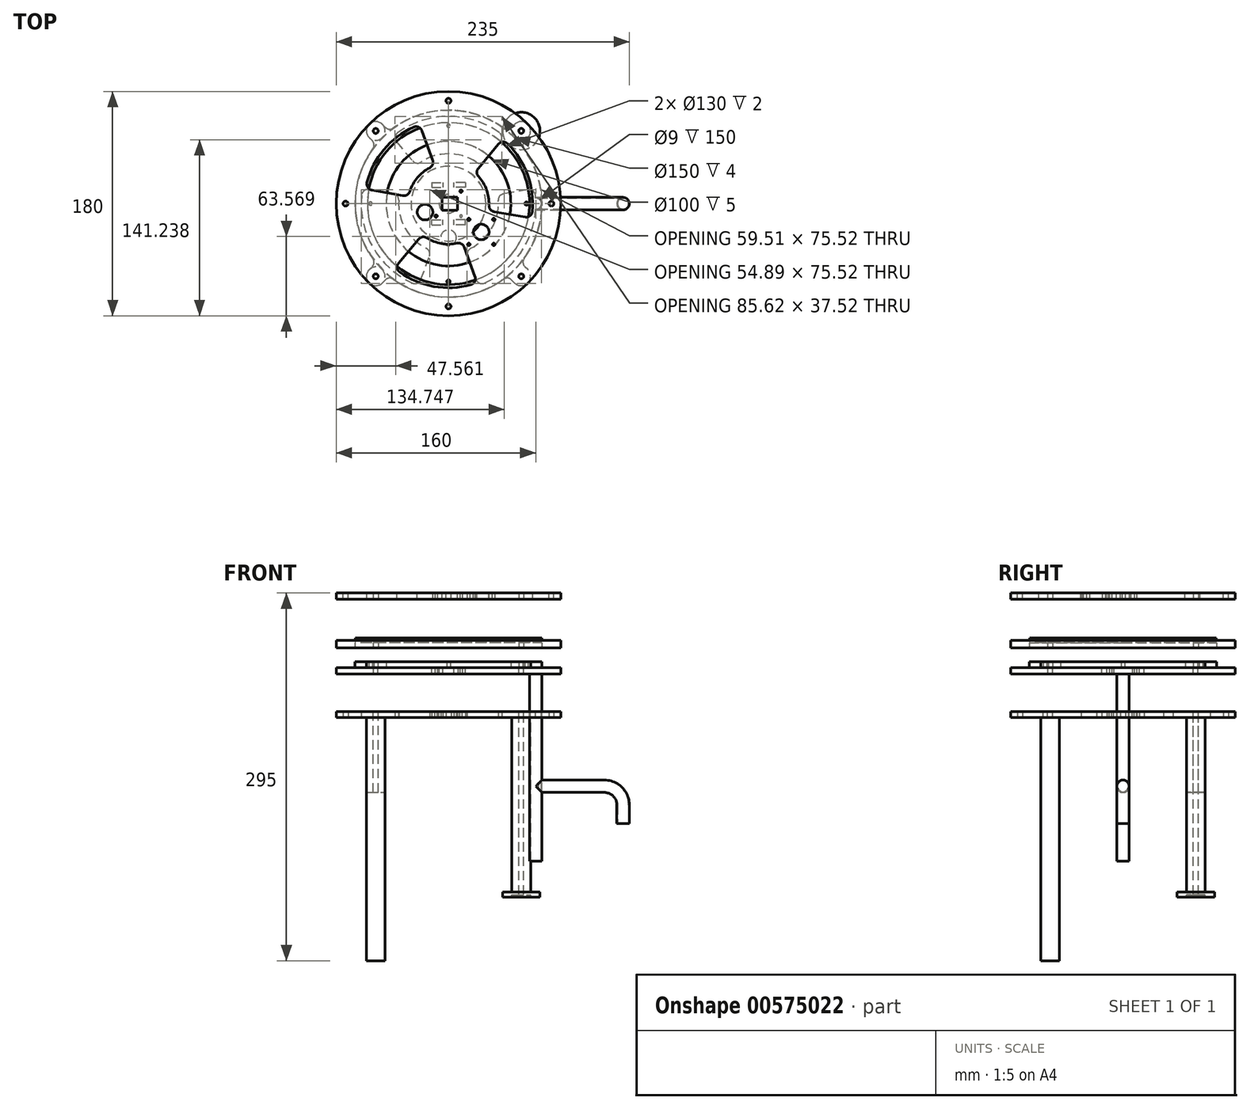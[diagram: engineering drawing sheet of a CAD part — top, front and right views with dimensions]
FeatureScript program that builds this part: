
annotation { "Feature Type Name" : "Feature", "Feature Type Description" : "" }
export const myFeature = defineFeature(function(context is Context, id is Id, definition is map)
    precondition{}
    {
        {
            var Q0;
            Q0=qCreatedBy(makeId("Top.planeOp"),FACE);
            var sketch = newSketch(context, id + "F0", { "sketchPlane" : qUnion([Q0])});
            skCircle(sketch, "E0", {"center": v(0, 0) * mm, "radius": 90 * mm});
            skCircle(sketch, "E1", {"center": v(0, 0) * mm, "radius": 75 * mm});
            skLineSegment(sketch, "E2", {"start": v(-75, 0) * mm, "end": v(-90, 0) * mm, "construction": true});
            skCircle(sketch, "E3", {"center": v(0, 0) * mm, "radius": 82.5 * mm, "construction": true});
            skPoint(sketch, "E4", {"position": v(-82.5, 0) * mm});
            skLineSegment(sketch, "E5", {"start": v(0, 0) * mm, "end": v(-58.34, 58.34) * mm, "construction": true});
            skCircle(sketch, "E6", {"center": v(-58.34, 58.34) * mm, "radius": 2 * mm});
            skCircle(sketch, "E7.MirrorC", {"center": v(58.34, 58.34) * mm, "radius": 2 * mm});
            skCircle(sketch, "E8.MirrorC", {"center": v(-58.34, -58.34) * mm, "radius": 2 * mm});
            skCircle(sketch, "E9.MirrorC", {"center": v(58.34, -58.34) * mm, "radius": 2 * mm});
            skSolve(sketch);
        }
        {
            var Q0;
            Q0=qSketchRegion(id+"F0",true);
            extrude(context, id + "F1", {"entities" : qUnion([Q0]), "depth" : 4 * mm, "offsetDistance" : 25 * mm});
        }
        {
            var Q0;
            Q0=makeQuery(id+"F1.opExtrude","CAP_FACE",FACE,{"disambiguationData":[OSD([sQuery(id+"F0.wireOp",EDGE,"E0"),sQuery(id+"F0.wireOp",EDGE,"E1"),sQuery(id+"F0.wireOp",EDGE,"E6"),sQuery(id+"F0.wireOp",EDGE,"E7.MirrorC"),sQuery(id+"F0.wireOp",EDGE,"E8.MirrorC"),sQuery(id+"F0.wireOp",EDGE,"E9.MirrorC")])],"isStart":true});
            cPlane(context, id + "F2", {"entities" : qUnion([Q0]), "cplaneType" : CPlaneType.OFFSET, "offset" : 1 * mm, "width" : 150 * mm, "height" : 150 * mm});
        }
        {
            var Q0;
            Q0=qCreatedBy(id+"F2.planeOp",FACE);
            var sketch = newSketch(context, id + "F3", { "sketchPlane" : qUnion([Q0])});
            skCircle(sketch, "E10.0", {"center": v(0, 0) * mm, "radius": 90 * mm});
            skCircle(sketch, "E11.0", {"center": v(-58.34, 58.34) * mm, "radius": 2 * mm});
            skCircle(sketch, "E12.0", {"center": v(58.34, 58.34) * mm, "radius": 2 * mm});
            skCircle(sketch, "E13.0", {"center": v(58.34, -58.34) * mm, "radius": 2 * mm});
            skCircle(sketch, "E14.0", {"center": v(-58.34, -58.34) * mm, "radius": 2 * mm});
            skCircle(sketch, "E15", {"center": v(0, 0) * mm, "radius": 7.55 * mm});
            skSolve(sketch);
        }
        {
            var Q0;
            Q0=qSketchRegion(id+"F3",true);
            extrude(context, id + "F4", {"entities" : qUnion([Q0]), "depth" : 5 * mm, "offsetDistance" : 25 * mm});
        }
        {
            var Q0;
            Q0=makeQuery(id+"F4.opExtrude","CAP_FACE",FACE,{"disambiguationData":[OSD([sQuery(id+"F3.wireOp",EDGE,"E10.0"),sQuery(id+"F3.wireOp",EDGE,"E11.0"),sQuery(id+"F3.wireOp",EDGE,"E12.0"),sQuery(id+"F3.wireOp",EDGE,"E13.0"),sQuery(id+"F3.wireOp",EDGE,"E14.0"),sQuery(id+"F3.wireOp",EDGE,"E15")])],"isStart":true});
            var sketch = newSketch(context, id + "F5", { "sketchPlane" : qUnion([Q0])});
            skLineSegment(sketch, "E16.bottom", {"start": v(-10, 10) * mm, "end": v(10, 10) * mm, "construction": true});
            skLineSegment(sketch, "E16.top", {"start": v(-10, -10) * mm, "end": v(10, -10) * mm, "construction": true});
            skLineSegment(sketch, "E16.left", {"start": v(-10, 10) * mm, "end": v(-10, -10) * mm, "construction": true});
            skLineSegment(sketch, "E16.right", {"start": v(10, 10) * mm, "end": v(10, -10) * mm, "construction": true});
            skPoint(sketch, "E16.middle", {"position": v(0, 0) * mm});
            skCircle(sketch, "E17", {"center": v(-10, 10) * mm, "radius": 1 * mm});
            skCircle(sketch, "E18.MirrorC", {"center": v(10, 10) * mm, "radius": 1 * mm});
            skCircle(sketch, "E19.MirrorC", {"center": v(-10, -10) * mm, "radius": 1 * mm});
            skCircle(sketch, "E20.MirrorC", {"center": v(10, -10) * mm, "radius": 1 * mm});
            skSolve(sketch);
        }
        {
            var Q0;
            Q0=qSketchRegion(id+"F5",true);
            extrude(context, id + "F6", {"entities" : qUnion([Q0]), "operationType" : NewBodyOperationType.REMOVE, "endBound" : BoundingType.UP_TO_NEXT, "oppositeDirection" : true, "depth" : 25 * mm, "offsetDistance" : 25 * mm});
        }
        {
            var Q0;
            Q0=makeQuery(id+"F4.opExtrude","CAP_FACE",FACE,{"disambiguationData":[OSD([sQuery(id+"F3.wireOp",EDGE,"E10.0"),sQuery(id+"F3.wireOp",EDGE,"E11.0"),sQuery(id+"F3.wireOp",EDGE,"E12.0"),sQuery(id+"F3.wireOp",EDGE,"E13.0"),sQuery(id+"F3.wireOp",EDGE,"E14.0"),sQuery(id+"F3.wireOp",EDGE,"E15")])],"isStart":false});
            var sketch = newSketch(context, id + "F7", { "sketchPlane" : qUnion([Q0])});
            skPoint(sketch, "E21.center", {"position": v(0, 0) * mm});
            skCircle(sketch, "E22", {"center": v(-58.34, 58.34) * mm, "radius": 7.5 * mm});
            skSolve(sketch);
        }
        {
            var Q0;
            Q0=qSketchRegion(id+"F7",true);
            extrude(context, id + "F8", {"entities" : qUnion([Q0]), "depth" : 195 * mm, "offsetDistance" : 25 * mm});
        }
        {
            var Q0;
            Q0=makeQuery(id+"F4.opExtrude","CAP_FACE",FACE,{"disambiguationData":[OSD([sQuery(id+"F3.wireOp",EDGE,"E10.0"),sQuery(id+"F3.wireOp",EDGE,"E11.0"),sQuery(id+"F3.wireOp",EDGE,"E12.0"),sQuery(id+"F3.wireOp",EDGE,"E13.0"),sQuery(id+"F3.wireOp",EDGE,"E14.0"),sQuery(id+"F3.wireOp",EDGE,"E15")])],"isStart":false});
            cPlane(context, id + "F9", {"entities" : qUnion([Q0]), "cplaneType" : CPlaneType.OFFSET, "offset" : 20 * mm, "oppositeDirection" : true, "width" : 150 * mm, "height" : 150 * mm});
        }
        {
            var Q0;
            Q0=makeQuery(id+"F4.opExtrude","SWEPT_BODY",BODY,{"disambiguationData":[OSD([sQuery(id+"F3.wireOp",EDGE,"E10.0"),sQuery(id+"F3.wireOp",EDGE,"E11.0"),sQuery(id+"F3.wireOp",EDGE,"E12.0"),sQuery(id+"F3.wireOp",EDGE,"E13.0"),sQuery(id+"F3.wireOp",EDGE,"E14.0"),sQuery(id+"F3.wireOp",EDGE,"E15")])]});
            var Q1;
            Q1=qCreatedBy(id+"F9.planeOp",FACE);
            mirror(context, id + "F10", {"entities" : qUnion([Q0]), "mirrorPlane" : qUnion([Q1])});
        }
        {
            var Q0;
            Q0=makeQuery(id+"F10.opPattern","COPY",FACE,{"derivedFrom":makeQuery(id+"F4.opExtrude","CAP_FACE",FACE,{"disambiguationData":[OSD([sQuery(id+"F3.wireOp",EDGE,"E10.0"),sQuery(id+"F3.wireOp",EDGE,"E11.0"),sQuery(id+"F3.wireOp",EDGE,"E12.0"),sQuery(id+"F3.wireOp",EDGE,"E13.0"),sQuery(id+"F3.wireOp",EDGE,"E14.0"),sQuery(id+"F3.wireOp",EDGE,"E15")])],"isStart":false}),"instanceName":"1"});
            var sketch = newSketch(context, id + "F11", { "sketchPlane" : qUnion([Q0])});
            skLineSegment(sketch, "E23.bottom", {"start": v(13, -13) * mm, "end": v(-13, -13) * mm, "construction": true});
            skLineSegment(sketch, "E23.top", {"start": v(13, -17) * mm, "end": v(-13, -17) * mm, "construction": true});
            skLineSegment(sketch, "E23.left", {"start": v(13, -13) * mm, "end": v(13, -17) * mm, "construction": true});
            skLineSegment(sketch, "E23.right", {"start": v(-13, -13) * mm, "end": v(-13, -17) * mm, "construction": true});
            skPoint(sketch, "E23.middle", {"position": v(0, -15) * mm});
            skLineSegment(sketch, "E24", {"start": v(5, -13) * mm, "end": v(5, -17) * mm, "construction": true});
            skLineSegment(sketch, "E25.MirrorCS", {"start": v(-5, -13) * mm, "end": v(-5, -17) * mm, "construction": true});
            skLineSegment(sketch, "E26", {"start": v(5, -13) * mm, "end": v(13, -17) * mm, "construction": true});
            skPoint(sketch, "E27", {"position": v(9, -15) * mm});
            skLineSegment(sketch, "E28.bottom", {"start": v(4.5, -13) * mm, "end": v(13.5, -13) * mm});
            skLineSegment(sketch, "E28.top", {"start": v(4.5, -17) * mm, "end": v(13.5, -17) * mm});
            skLineSegment(sketch, "E28.left", {"start": v(4.5, -13) * mm, "end": v(4.5, -17) * mm});
            skLineSegment(sketch, "E28.right", {"start": v(13.5, -13) * mm, "end": v(13.5, -17) * mm});
            skLineSegment(sketch, "E29.MirrorCS", {"start": v(-4.5, -13) * mm, "end": v(-4.5, -17) * mm});
            skLineSegment(sketch, "E30.MirrorCS", {"start": v(-4.5, -13) * mm, "end": v(-13.5, -13) * mm});
            skLineSegment(sketch, "E31.MirrorCS", {"start": v(-13.5, -13) * mm, "end": v(-13.5, -17) * mm});
            skLineSegment(sketch, "E32.MirrorCS", {"start": v(-4.5, -17) * mm, "end": v(-13.5, -17) * mm});
            skLineSegment(sketch, "E33.MirrorCS", {"start": v(-13.5, 13) * mm, "end": v(-13.5, 17) * mm});
            skLineSegment(sketch, "E34.MirrorCS", {"start": v(-4.5, 13) * mm, "end": v(-13.5, 13) * mm});
            skLineSegment(sketch, "E35.MirrorCS", {"start": v(-4.5, 13) * mm, "end": v(-4.5, 17) * mm});
            skLineSegment(sketch, "E36.MirrorCS", {"start": v(-4.5, 17) * mm, "end": v(-13.5, 17) * mm});
            skLineSegment(sketch, "E37.MirrorCS", {"start": v(4.5, 13) * mm, "end": v(4.5, 17) * mm});
            skLineSegment(sketch, "E38.MirrorCS", {"start": v(4.5, 13) * mm, "end": v(13.5, 13) * mm});
            skLineSegment(sketch, "E39.MirrorCS", {"start": v(13.5, 13) * mm, "end": v(13.5, 17) * mm});
            skLineSegment(sketch, "E40.MirrorCS", {"start": v(4.5, 17) * mm, "end": v(13.5, 17) * mm});
            skSolve(sketch);
        }
        {
            var Q0;
            Q0=qSketchRegion(id+"F11",true);
            extrude(context, id + "F12", {"entities" : qUnion([Q0]), "operationType" : NewBodyOperationType.REMOVE, "endBound" : BoundingType.UP_TO_NEXT, "oppositeDirection" : true, "depth" : 25 * mm, "offsetDistance" : 25 * mm});
        }
        {
            var Q0;
            Q0=makeQuery(id+"F10.opPattern","COPY",FACE,{"derivedFrom":makeQuery(id+"F4.opExtrude","CAP_FACE",FACE,{"disambiguationData":[OSD([sQuery(id+"F3.wireOp",EDGE,"E10.0"),sQuery(id+"F3.wireOp",EDGE,"E11.0"),sQuery(id+"F3.wireOp",EDGE,"E12.0"),sQuery(id+"F3.wireOp",EDGE,"E13.0"),sQuery(id+"F3.wireOp",EDGE,"E14.0"),sQuery(id+"F3.wireOp",EDGE,"E15")])],"isStart":false}),"instanceName":"1"});
            var sketch = newSketch(context, id + "F13", { "sketchPlane" : qUnion([Q0])});
            skCircle(sketch, "E41", {"center": v(-58.34, 58.34) * mm, "radius": 1.85 * mm});
            skCircle(sketch, "E42.0", {"center": v(-58.34, 58.34) * mm, "radius": 2 * mm});
            skCircle(sketch, "E43.1.0", {"center": v(-58.34, -58.34) * mm, "radius": 1.85 * mm});
            skCircle(sketch, "E43.1.1", {"center": v(-58.34, -58.34) * mm, "radius": 2 * mm});
            skCircle(sketch, "E43.2.0", {"center": v(58.34, -58.34) * mm, "radius": 1.85 * mm});
            skCircle(sketch, "E43.2.1", {"center": v(58.34, -58.34) * mm, "radius": 2 * mm});
            skCircle(sketch, "E43.3.0", {"center": v(58.34, 58.34) * mm, "radius": 1.85 * mm});
            skCircle(sketch, "E43.3.1", {"center": v(58.34, 58.34) * mm, "radius": 2 * mm});
            skPoint(sketch, "E43.center", {"position": v(0, 0) * mm});
            skSolve(sketch);
        }
        {
            var Q0;
            Q0=qSketchRegion(id+"F13",true);
            var Q1;
            Q1=makeQuery(id+"F10.opPattern","COPY",FACE,{"derivedFrom":makeQuery(id+"F4.opExtrude","CAP_FACE",FACE,{"disambiguationData":[OSD([sQuery(id+"F3.wireOp",EDGE,"E10.0"),sQuery(id+"F3.wireOp",EDGE,"E11.0"),sQuery(id+"F3.wireOp",EDGE,"E12.0"),sQuery(id+"F3.wireOp",EDGE,"E13.0"),sQuery(id+"F3.wireOp",EDGE,"E14.0"),sQuery(id+"F3.wireOp",EDGE,"E15")])],"isStart":true}),"instanceName":"1"});
            extrude(context, id + "F14", {"entities" : qUnion([Q0]), "operationType" : NewBodyOperationType.ADD, "endBound" : BoundingType.UP_TO_SURFACE, "oppositeDirection" : true, "depth" : 25 * mm, "endBoundEntityFace" : qUnion([Q1]), "offsetDistance" : 25 * mm});
        }
        {
            var Q0;
            Q0=makeQuery(id+"F14.boolean.opBoolean","MERGE",FACE,{"derivedFrom":[makeQuery(id+"F10.opPattern","COPY",FACE,{"derivedFrom":makeQuery(id+"F4.opExtrude","CAP_FACE",FACE,{"disambiguationData":[OSD([sQuery(id+"F3.wireOp",EDGE,"E10.0"),sQuery(id+"F3.wireOp",EDGE,"E11.0"),sQuery(id+"F3.wireOp",EDGE,"E12.0"),sQuery(id+"F3.wireOp",EDGE,"E13.0"),sQuery(id+"F3.wireOp",EDGE,"E14.0"),sQuery(id+"F3.wireOp",EDGE,"E15")])],"isStart":false}),"instanceName":"1"}),makeQuery(id+"F14.opExtrude","CAP_FACE",FACE,{"disambiguationData":[OSD([sQuery(id+"F13.wireOp",EDGE,"E41"),sQuery(id+"F13.wireOp",EDGE,"E42.0")])],"isStart":true}),makeQuery(id+"F14.opExtrude","CAP_FACE",FACE,{"disambiguationData":[OSD([sQuery(id+"F13.wireOp",EDGE,"E43.1.0"),sQuery(id+"F13.wireOp",EDGE,"E43.1.1")])],"isStart":true}),makeQuery(id+"F14.opExtrude","CAP_FACE",FACE,{"disambiguationData":[OSD([sQuery(id+"F13.wireOp",EDGE,"E43.2.0"),sQuery(id+"F13.wireOp",EDGE,"E43.2.1")])],"isStart":true}),makeQuery(id+"F14.opExtrude","CAP_FACE",FACE,{"disambiguationData":[OSD([sQuery(id+"F13.wireOp",EDGE,"E43.3.0"),sQuery(id+"F13.wireOp",EDGE,"E43.3.1")])],"isStart":true})]});
            var sketch = newSketch(context, id + "F15", { "sketchPlane" : qUnion([Q0])});
            skCircle(sketch, "E44.0", {"center": v(-58.34, 58.34) * mm, "radius": 1.85 * mm});
            skCircle(sketch, "E45.0", {"center": v(-58.34, -58.34) * mm, "radius": 1.85 * mm});
            skCircle(sketch, "E46.0", {"center": v(58.34, -58.34) * mm, "radius": 1.85 * mm});
            skCircle(sketch, "E47.0", {"center": v(58.34, 58.34) * mm, "radius": 1.85 * mm});
            skArc(sketch, "E48", {"start": v(63.64, 53.03) * mm, "mid": v(63.64, 63.64) * mm, "end": v(53.03, 63.64) * mm});
            skCircle(sketch, "E49", {"center": v(0, 0) * mm, "radius": 50 * mm});
            skArc(sketch, "E50", {"start": v(47.46, 58.07) * mm, "mid": v(0, 75) * mm, "end": v(-47.46, 58.07) * mm});
            skLineSegment(sketch, "E51", {"start": v(58.34, 58.34) * mm, "end": v(63.64, 53.03) * mm, "construction": true});
            skLineSegment(sketch, "E52", {"start": v(58.34, 58.34) * mm, "end": v(0, 0) * mm, "construction": true});
            skLineSegment(sketch, "E53", {"start": v(63.64, 53.03) * mm, "end": v(58.07, 47.46) * mm});
            skLineSegment(sketch, "E54.MirrorCS", {"start": v(53.03, 63.64) * mm, "end": v(47.46, 58.07) * mm});
            skLineSegment(sketch, "E55.MirrorCS", {"start": v(-53.03, 63.64) * mm, "end": v(-47.46, 58.07) * mm});
            skArc(sketch, "E56.MirrorCS", {"start": v(-63.64, 53.03) * mm, "mid": v(-63.64, 63.64) * mm, "end": v(-53.03, 63.64) * mm});
            skLineSegment(sketch, "E57.MirrorCS", {"start": v(-63.64, 53.03) * mm, "end": v(-58.07, 47.46) * mm});
            skLineSegment(sketch, "E58.MirrorCS", {"start": v(58.34, -58.34) * mm, "end": v(59.64, -57.03) * mm, "construction": true});
            skLineSegment(sketch, "E59.MirrorCS", {"start": v(-63.64, -53.03) * mm, "end": v(-58.07, -47.46) * mm});
            skLineSegment(sketch, "E60.MirrorCS", {"start": v(63.64, -53.03) * mm, "end": v(58.07, -47.46) * mm});
            skArc(sketch, "E61.MirrorCS", {"start": v(63.64, -53.03) * mm, "mid": v(63.64, -63.64) * mm, "end": v(53.03, -63.64) * mm});
            skLineSegment(sketch, "E62.MirrorCS", {"start": v(53.03, -63.64) * mm, "end": v(47.46, -58.07) * mm});
            skLineSegment(sketch, "E63.MirrorCS", {"start": v(-53.03, -63.64) * mm, "end": v(-47.46, -58.07) * mm});
            skArc(sketch, "E64.MirrorCS", {"start": v(-63.64, -53.03) * mm, "mid": v(-63.64, -63.64) * mm, "end": v(-53.03, -63.64) * mm});
            skArc(sketch, "E65.trimOffspring", {"start": v(-58.07, 47.46) * mm, "mid": v(-75, 0) * mm, "end": v(-58.07, -47.46) * mm});
            skArc(sketch, "E66.trimOffspring", {"start": v(-47.46, -58.07) * mm, "mid": v(0, -75) * mm, "end": v(47.46, -58.07) * mm});
            skArc(sketch, "E67.trimOffspring", {"start": v(58.07, -47.46) * mm, "mid": v(75, 0) * mm, "end": v(58.07, 47.46) * mm});
            skCircle(sketch, "E68", {"center": v(0, 62.5) * mm, "radius": 1.35 * mm});
            skCircle(sketch, "E69.1.0", {"center": v(-62.5, 0) * mm, "radius": 1.35 * mm});
            skCircle(sketch, "E69.2.0", {"center": v(0, -62.5) * mm, "radius": 1.35 * mm});
            skCircle(sketch, "E70.1.3.0", {"center": v(62.5, 0) * mm, "radius": 1.35 * mm});
            skSolve(sketch);
        }
        {
            var Q0;
            Q0=qSketchRegion(id+"F15",true);
            extrude(context, id + "F16", {"entities" : qUnion([Q0]), "depth" : 5 * mm, "offsetDistance" : 25 * mm});
        }
        {
            var Q0;
            Q0=makeQuery(id+"F16.opExtrude","SWEPT_EDGE",EDGE,{"disambiguationData":[OSD([sQuery(id+"F15.wireOp",EDGE,"E50"),sQuery(id+"F15.wireOp",EDGE,"E55.MirrorCS")])]});
            var Q1;
            Q1=makeQuery(id+"F16.opExtrude","SWEPT_EDGE",EDGE,{"disambiguationData":[OSD([sQuery(id+"F15.wireOp",EDGE,"E50"),sQuery(id+"F15.wireOp",EDGE,"E54.MirrorCS")])]});
            var Q2;
            Q2=makeQuery(id+"F16.opExtrude","SWEPT_EDGE",EDGE,{"disambiguationData":[OSD([sQuery(id+"F15.wireOp",EDGE,"E53"),sQuery(id+"F15.wireOp",EDGE,"E67.trimOffspring")])]});
            var Q3;
            Q3=makeQuery(id+"F16.opExtrude","SWEPT_EDGE",EDGE,{"disambiguationData":[OSD([sQuery(id+"F15.wireOp",EDGE,"E60.MirrorCS"),sQuery(id+"F15.wireOp",EDGE,"E67.trimOffspring")])]});
            var Q4;
            Q4=makeQuery(id+"F16.opExtrude","SWEPT_EDGE",EDGE,{"disambiguationData":[OSD([sQuery(id+"F15.wireOp",EDGE,"E62.MirrorCS"),sQuery(id+"F15.wireOp",EDGE,"E66.trimOffspring")])]});
            var Q5;
            Q5=makeQuery(id+"F16.opExtrude","SWEPT_EDGE",EDGE,{"disambiguationData":[OSD([sQuery(id+"F15.wireOp",EDGE,"E63.MirrorCS"),sQuery(id+"F15.wireOp",EDGE,"E66.trimOffspring")])]});
            var Q6;
            Q6=makeQuery(id+"F16.opExtrude","SWEPT_EDGE",EDGE,{"disambiguationData":[OSD([sQuery(id+"F15.wireOp",EDGE,"E59.MirrorCS"),sQuery(id+"F15.wireOp",EDGE,"E65.trimOffspring")])]});
            var Q7;
            Q7=makeQuery(id+"F16.opExtrude","SWEPT_EDGE",EDGE,{"disambiguationData":[OSD([sQuery(id+"F15.wireOp",EDGE,"E57.MirrorCS"),sQuery(id+"F15.wireOp",EDGE,"E65.trimOffspring")])]});
            fillet(context, id + "F17", {"entities" : qUnion([Q0, Q1, Q2, Q3, Q4, Q5, Q6, Q7]), "radius" : 5 * mm, "tangentPropagation" : true, "allowEdgeOverflow" : false});
        }
        {
            var Q0;
            Q0=makeQuery(id+"F4.opExtrude","CAP_FACE",FACE,{"disambiguationData":[OSD([sQuery(id+"F3.wireOp",EDGE,"E10.0"),sQuery(id+"F3.wireOp",EDGE,"E11.0"),sQuery(id+"F3.wireOp",EDGE,"E12.0"),sQuery(id+"F3.wireOp",EDGE,"E13.0"),sQuery(id+"F3.wireOp",EDGE,"E14.0"),sQuery(id+"F3.wireOp",EDGE,"E15")])],"isStart":false});
            var sketch = newSketch(context, id + "F18", { "sketchPlane" : qUnion([Q0])});
            skCircle(sketch, "E71", {"center": v(58.34, -58.34) * mm, "radius": 7.5 * mm});
            skCircle(sketch, "E72.0", {"center": v(58.34, -58.34) * mm, "radius": 2 * mm});
            skSolve(sketch);
        }
        {
            var Q0;
            Q0=qSketchRegion(id+"F18",true);
            extrude(context, id + "F19", {"entities" : qUnion([Q0]), "depth" : 140 * mm, "offsetDistance" : 25 * mm});
        }
        {
            var Q0;
            Q0=makeQuery(id+"F19.opExtrude","CAP_FACE",FACE,{"disambiguationData":[OSD([sQuery(id+"F18.wireOp",EDGE,"E71"),sQuery(id+"F18.wireOp",EDGE,"E72.0")])],"isStart":false});
            var sketch = newSketch(context, id + "F20", { "sketchPlane" : qUnion([Q0])});
            skCircle(sketch, "E73.0", {"center": v(58.34, -58.34) * mm, "radius": 7.5 * mm});
            skCircle(sketch, "E74.0", {"center": v(58.34, -58.34) * mm, "radius": 2 * mm});
            skCircle(sketch, "E75", {"center": v(58.34, -58.34) * mm, "radius": 15 * mm});
            skSolve(sketch);
        }
        {
            var Q0;
            Q0=makeQuery(id+"F20.imprint","IMPRINT",FACE,{"disambiguationData":[TD([[makeQuery(id+"F20.imprint","IMPRINT",EDGE,{"derivedFrom":sQuery(id+"F20.wireOp",EDGE,"E73.0")}),-1.0]])]});
            extrude(context, id + "F21", {"entities" : qUnion([Q0]), "depth" : 4 * mm, "offsetDistance" : 25 * mm});
        }
        {
            var Q0;
            Q0=makeQuery(id+"F19.opExtrude","CAP_FACE",FACE,{"disambiguationData":[OSD([sQuery(id+"F18.wireOp",EDGE,"E71"),sQuery(id+"F18.wireOp",EDGE,"E72.0")])],"isStart":false});
            extrude(context, id + "F22", {"entities" : qUnion([Q0]), "operationType" : NewBodyOperationType.ADD, "depth" : 2 * mm, "offsetDistance" : 25 * mm});
        }
        {
            var Q0;
            Q0=makeQuery(id+"F14.boolean.opBoolean","MERGE",FACE,{"derivedFrom":[makeQuery(id+"F10.opPattern","COPY",FACE,{"derivedFrom":makeQuery(id+"F4.opExtrude","CAP_FACE",FACE,{"disambiguationData":[OSD([sQuery(id+"F3.wireOp",EDGE,"E10.0"),sQuery(id+"F3.wireOp",EDGE,"E11.0"),sQuery(id+"F3.wireOp",EDGE,"E12.0"),sQuery(id+"F3.wireOp",EDGE,"E13.0"),sQuery(id+"F3.wireOp",EDGE,"E14.0"),sQuery(id+"F3.wireOp",EDGE,"E15")])],"isStart":false}),"instanceName":"1"}),makeQuery(id+"F14.opExtrude","CAP_FACE",FACE,{"disambiguationData":[OSD([sQuery(id+"F13.wireOp",EDGE,"E41"),sQuery(id+"F13.wireOp",EDGE,"E42.0")])],"isStart":true}),makeQuery(id+"F14.opExtrude","CAP_FACE",FACE,{"disambiguationData":[OSD([sQuery(id+"F13.wireOp",EDGE,"E43.1.0"),sQuery(id+"F13.wireOp",EDGE,"E43.1.1")])],"isStart":true}),makeQuery(id+"F14.opExtrude","CAP_FACE",FACE,{"disambiguationData":[OSD([sQuery(id+"F13.wireOp",EDGE,"E43.2.0"),sQuery(id+"F13.wireOp",EDGE,"E43.2.1")])],"isStart":true}),makeQuery(id+"F14.opExtrude","CAP_FACE",FACE,{"disambiguationData":[OSD([sQuery(id+"F13.wireOp",EDGE,"E43.3.0"),sQuery(id+"F13.wireOp",EDGE,"E43.3.1")])],"isStart":true})]});
            cPlane(context, id + "F23", {"entities" : qUnion([Q0]), "cplaneType" : CPlaneType.OFFSET, "offset" : 10 * mm, "width" : 150 * mm, "height" : 150 * mm});
        }
        {
            var Q0;
            Q0=makeQuery(id+"F4.opExtrude","SWEPT_BODY",BODY,{"disambiguationData":[OSD([sQuery(id+"F3.wireOp",EDGE,"E10.0"),sQuery(id+"F3.wireOp",EDGE,"E11.0"),sQuery(id+"F3.wireOp",EDGE,"E12.0"),sQuery(id+"F3.wireOp",EDGE,"E13.0"),sQuery(id+"F3.wireOp",EDGE,"E14.0"),sQuery(id+"F3.wireOp",EDGE,"E15")])]});
            var Q1;
            Q1=qCreatedBy(id+"F23.planeOp",FACE);
            mirror(context, id + "F24", {"entities" : qUnion([Q0]), "mirrorPlane" : qUnion([Q1])});
        }
        {
            var Q0;
            Q0=makeQuery(id+"F24.opPattern","COPY",FACE,{"derivedFrom":makeQuery(id+"F4.opExtrude","CAP_FACE",FACE,{"disambiguationData":[OSD([sQuery(id+"F3.wireOp",EDGE,"E10.0"),sQuery(id+"F3.wireOp",EDGE,"E11.0"),sQuery(id+"F3.wireOp",EDGE,"E12.0"),sQuery(id+"F3.wireOp",EDGE,"E13.0"),sQuery(id+"F3.wireOp",EDGE,"E14.0"),sQuery(id+"F3.wireOp",EDGE,"E15")])],"isStart":false}),"instanceName":"1"});
            var sketch = newSketch(context, id + "F25", { "sketchPlane" : qUnion([Q0])});
            skCircle(sketch, "E76.0", {"center": v(-10, -10) * mm, "radius": 1 * mm});
            skCircle(sketch, "E77.0", {"center": v(-10, 10) * mm, "radius": 1 * mm});
            skCircle(sketch, "E78.0", {"center": v(10, 10) * mm, "radius": 1 * mm});
            skCircle(sketch, "E79.0", {"center": v(10, -10) * mm, "radius": 1 * mm});
            skLineSegment(sketch, "E80.bottom", {"start": v(16.3, -12.75) * mm, "end": v(36.3, -12.75) * mm, "construction": true});
            skLineSegment(sketch, "E80.top", {"start": v(16.3, -32.75) * mm, "end": v(36.3, -32.75) * mm, "construction": true});
            skLineSegment(sketch, "E80.left", {"start": v(16.3, -12.75) * mm, "end": v(16.3, -32.75) * mm, "construction": true});
            skLineSegment(sketch, "E80.right", {"start": v(36.3, -12.75) * mm, "end": v(36.3, -32.75) * mm, "construction": true});
            skPoint(sketch, "E80.middle", {"position": v(26.3, -22.75) * mm});
            skCircle(sketch, "E81", {"center": v(36.3, -12.75) * mm, "radius": 1 * mm});
            skCircle(sketch, "E82.1.0", {"center": v(16.3, -12.75) * mm, "radius": 1 * mm});
            skCircle(sketch, "E82.2.0", {"center": v(16.3, -32.75) * mm, "radius": 1 * mm});
            skCircle(sketch, "E83.1.3.0", {"center": v(36.3, -32.75) * mm, "radius": 1 * mm});
            skCircle(sketch, "E84", {"center": v(26.3, -22.75) * mm, "radius": 6.25 * mm});
            skCircle(sketch, "E85.0", {"center": v(-58.34, 58.34) * mm, "radius": 2 * mm});
            skCircle(sketch, "E86.1.0", {"center": v(-82.5, 0) * mm, "radius": 2 * mm});
            skCircle(sketch, "E86.2.0", {"center": v(-58.34, -58.34) * mm, "radius": 2 * mm});
            skCircle(sketch, "E87.1.3.0", {"center": v(0, -82.5) * mm, "radius": 2 * mm});
            skCircle(sketch, "E87.1.4.0", {"center": v(58.34, -58.34) * mm, "radius": 2 * mm});
            skCircle(sketch, "E87.1.5.0", {"center": v(82.5, 0) * mm, "radius": 2 * mm});
            skCircle(sketch, "E87.1.6.0", {"center": v(58.34, 58.34) * mm, "radius": 2 * mm});
            skCircle(sketch, "E87.1.7.0", {"center": v(0, 82.5) * mm, "radius": 2 * mm});
            skLineSegment(sketch, "E88.bottom", {"start": v(-5.25, 5.25) * mm, "end": v(7.25, 5.25) * mm});
            skLineSegment(sketch, "E88.top", {"start": v(-5.25, -5.25) * mm, "end": v(7.25, -5.25) * mm});
            skLineSegment(sketch, "E88.left", {"start": v(-5.25, 5.25) * mm, "end": v(-5.25, -5.25) * mm});
            skLineSegment(sketch, "E88.right", {"start": v(7.25, 5.25) * mm, "end": v(7.25, -5.25) * mm});
            skPoint(sketch, "E88.middle", {"position": v(1, 0) * mm});
            skSolve(sketch);
        }
        {
            var Q0;
            {var subQ0=sQuery(id+"F25.wireOp",EDGE,"QSQis5DJ-ndRP-tXz9-sWgT-VjHo9YrmBDyp.right");var subQ1=sQuery(id+"F25.wireOp",EDGE,"15366a01-08b8-4944-8cce-0e4f2887150d.0");var subQ2=makeQuery(id+"F25.imprint","INTERSECT",VERTEX,{"disambiguationData":[OD(0.0)],"derivedFrom":[subQ1,subQ0]});Q0=makeQuery(id+"F25.imprint","IMPRINT",FACE,{"disambiguationData":[TD([[makeQuery(id+"F25.imprint","IMPRINT",EDGE,{"disambiguationData":[TD([[subQ2,1.0]])],"derivedFrom":subQ1}),-1.0]])]});}
            var Q1;
            Q1=makeQuery(id+"F25.imprint","IMPRINT",FACE,{"disambiguationData":[TD([[makeQuery(id+"F25.imprint","IMPRINT",EDGE,{"derivedFrom":sQuery(id+"F25.wireOp",EDGE,"E77.0")}),1.0]])]});
            var Q2;
            Q2=makeQuery(id+"F25.imprint","IMPRINT",FACE,{"disambiguationData":[TD([[makeQuery(id+"F25.imprint","IMPRINT",EDGE,{"derivedFrom":sQuery(id+"F25.wireOp",EDGE,"E78.0")}),-1.0]])]});
            var Q3;
            Q3=makeQuery(id+"F25.imprint","IMPRINT",FACE,{"disambiguationData":[TD([[makeQuery(id+"F25.imprint","IMPRINT",EDGE,{"derivedFrom":sQuery(id+"F25.wireOp",EDGE,"E79.0")}),1.0]])]});
            var Q4;
            Q4=makeQuery(id+"F25.imprint","IMPRINT",FACE,{"disambiguationData":[TD([[makeQuery(id+"F25.imprint","IMPRINT",EDGE,{"derivedFrom":sQuery(id+"F25.wireOp",EDGE,"E76.0")}),-1.0]])]});
            var Q5;
            {var subQ0=sQuery(id+"F25.wireOp",EDGE,"QSQis5DJ-ndRP-tXz9-sWgT-VjHo9YrmBDyp.left");var subQ1=sQuery(id+"F25.wireOp",EDGE,"15366a01-08b8-4944-8cce-0e4f2887150d.0");var subQ2=makeQuery(id+"F25.imprint","INTERSECT",VERTEX,{"disambiguationData":[OD(0.0)],"derivedFrom":[subQ1,subQ0]});Q5=makeQuery(id+"F25.imprint","IMPRINT",FACE,{"disambiguationData":[TD([[makeQuery(id+"F25.imprint","IMPRINT",EDGE,{"disambiguationData":[TD([[subQ2,-1.0]])],"derivedFrom":subQ1}),-1.0]])]});}
            var Q6;
            {var subQ0=sQuery(id+"F25.wireOp",EDGE,"QSQis5DJ-ndRP-tXz9-sWgT-VjHo9YrmBDyp.bottom");var subQ1=sQuery(id+"F25.wireOp",EDGE,"15366a01-08b8-4944-8cce-0e4f2887150d.0");var subQ2=makeQuery(id+"F25.imprint","INTERSECT",VERTEX,{"disambiguationData":[OD(0.0)],"derivedFrom":[subQ1,subQ0]});Q6=makeQuery(id+"F25.imprint","IMPRINT",FACE,{"disambiguationData":[TD([[makeQuery(id+"F25.imprint","IMPRINT",EDGE,{"disambiguationData":[TD([[subQ2,-1.0]])],"derivedFrom":subQ1}),-1.0]])]});}
            var Q7;
            {var subQ0=sQuery(id+"F25.wireOp",EDGE,"QSQis5DJ-ndRP-tXz9-sWgT-VjHo9YrmBDyp.top");var subQ1=sQuery(id+"F25.wireOp",EDGE,"15366a01-08b8-4944-8cce-0e4f2887150d.0");var subQ2=makeQuery(id+"F25.imprint","INTERSECT",VERTEX,{"disambiguationData":[OD(0.0)],"derivedFrom":[subQ1,subQ0]});Q7=makeQuery(id+"F25.imprint","IMPRINT",FACE,{"disambiguationData":[TD([[makeQuery(id+"F25.imprint","IMPRINT",EDGE,{"disambiguationData":[TD([[subQ2,-1.0]])],"derivedFrom":subQ1}),-1.0]])]});}
            var Q8;
            {var subQ0=sQuery(id+"F25.wireOp",EDGE,"E88.left");Q8=makeQuery(id+"F25.imprint","IMPRINT",FACE,{"disambiguationData":[TD([[makeQuery(id+"F25.imprint","IMPRINT",EDGE,{"derivedFrom":subQ0}),-1.0]])]});}
            var Q9;
            {var subQ0=sQuery(id+"F25.wireOp",EDGE,"E88.right");var subQ1=makeQuery(id+"F24.opPattern","COPY",EDGE,{"derivedFrom":makeQuery(id+"F4.opExtrude","CAP_EDGE",EDGE,{"disambiguationData":[OSD([sQuery(id+"F3.wireOp",EDGE,"E15")])],"isStart":false}),"instanceName":"1"});var subQ2=makeQuery(id+"F25.imprint","INTERSECT",VERTEX,{"disambiguationData":[OD(0.0)],"derivedFrom":[subQ1,subQ0]});Q9=makeQuery(id+"F25.imprint","IMPRINT",FACE,{"disambiguationData":[TD([[makeQuery(id+"F25.imprint","IMPRINT",EDGE,{"disambiguationData":[TD([[subQ2,-1.0]])],"derivedFrom":subQ0}),1.0]])]});}
            extrude(context, id + "F26", {"entities" : qUnion([Q0, Q1, Q2, Q3, Q4, Q5, Q6, Q7, Q8, Q9]), "operationType" : NewBodyOperationType.ADD, "oppositeDirection" : true, "depth" : 5 * mm, "offsetDistance" : 25 * mm});
        }
        {
            var Q0;
            {var subQ5=sQuery(id+"F25.wireOp",EDGE,"656fdb2e-e72c-4114-8cef-4688475ef528.filletArc");Q0=makeQuery(id+"F25.imprint","IMPRINT",FACE,{"disambiguationData":[TD([[makeQuery(id+"F25.imprint","IMPRINT",EDGE,{"derivedFrom":subQ5}),1.0]])]});}
            var Q1;
            {var subQ5=sQuery(id+"F25.wireOp",EDGE,"dae69112-de24-48df-9be6-64b79decc6ef.filletArc");Q1=makeQuery(id+"F25.imprint","IMPRINT",FACE,{"disambiguationData":[TD([[makeQuery(id+"F25.imprint","IMPRINT",EDGE,{"derivedFrom":subQ5}),1.0]])]});}
            var Q2;
            {var subQ5=sQuery(id+"F25.wireOp",EDGE,"470e9d0d-4a14-41c7-af53-fb42cd5c9400.filletArc");Q2=makeQuery(id+"F25.imprint","IMPRINT",FACE,{"disambiguationData":[TD([[makeQuery(id+"F25.imprint","IMPRINT",EDGE,{"derivedFrom":subQ5}),1.0]])]});}
            var Q3;
            {var subQ5=sQuery(id+"F25.wireOp",EDGE,"ee6f9c0c-4a7c-40b4-91d3-26762448eaf5.filletArc");Q3=makeQuery(id+"F25.imprint","IMPRINT",FACE,{"disambiguationData":[TD([[makeQuery(id+"F25.imprint","IMPRINT",EDGE,{"derivedFrom":subQ5}),1.0]])]});}
            var Q4;
            Q4=makeQuery(id+"F25.imprint","IMPRINT",FACE,{"disambiguationData":[TD([[makeQuery(id+"F25.imprint","IMPRINT",EDGE,{"derivedFrom":sQuery(id+"F25.wireOp",EDGE,"E84")}),1.0]])]});
            var Q5;
            Q5=makeQuery(id+"F25.imprint","IMPRINT",FACE,{"disambiguationData":[TD([[makeQuery(id+"F25.imprint","IMPRINT",EDGE,{"derivedFrom":sQuery(id+"F25.wireOp",EDGE,"E81")}),1.0]])]});
            var Q6;
            Q6=makeQuery(id+"F25.imprint","IMPRINT",FACE,{"disambiguationData":[TD([[makeQuery(id+"F25.imprint","IMPRINT",EDGE,{"derivedFrom":sQuery(id+"F25.wireOp",EDGE,"E83.1.3.0")}),1.0]])]});
            var Q7;
            Q7=makeQuery(id+"F25.imprint","IMPRINT",FACE,{"disambiguationData":[TD([[makeQuery(id+"F25.imprint","IMPRINT",EDGE,{"derivedFrom":sQuery(id+"F25.wireOp",EDGE,"E82.2.0")}),1.0]])]});
            var Q8;
            Q8=makeQuery(id+"F25.imprint","IMPRINT",FACE,{"disambiguationData":[TD([[makeQuery(id+"F25.imprint","IMPRINT",EDGE,{"derivedFrom":sQuery(id+"F25.wireOp",EDGE,"E82.1.0")}),1.0]])]});
            var Q9;
            {var subQ0=sQuery(id+"F25.wireOp",EDGE,"QSQis5DJ-ndRP-tXz9-sWgT-VjHo9YrmBDyp.bottom");var subQ1=sQuery(id+"F25.wireOp",EDGE,"15366a01-08b8-4944-8cce-0e4f2887150d.0");var subQ2=makeQuery(id+"F25.imprint","INTERSECT",VERTEX,{"disambiguationData":[OD(1.0)],"derivedFrom":[subQ1,subQ0]});Q9=makeQuery(id+"F25.imprint","IMPRINT",FACE,{"disambiguationData":[TD([[makeQuery(id+"F25.imprint","IMPRINT",EDGE,{"disambiguationData":[TD([[subQ2,-1.0]])],"derivedFrom":subQ1}),1.0]])]});}
            var Q10;
            {var subQ0=sQuery(id+"F25.wireOp",EDGE,"QSQis5DJ-ndRP-tXz9-sWgT-VjHo9YrmBDyp.top");var subQ1=sQuery(id+"F25.wireOp",EDGE,"15366a01-08b8-4944-8cce-0e4f2887150d.0");var subQ2=makeQuery(id+"F25.imprint","INTERSECT",VERTEX,{"disambiguationData":[OD(0.0)],"derivedFrom":[subQ1,subQ0]});Q10=makeQuery(id+"F25.imprint","IMPRINT",FACE,{"disambiguationData":[TD([[makeQuery(id+"F25.imprint","IMPRINT",EDGE,{"disambiguationData":[TD([[subQ2,1.0]])],"derivedFrom":subQ1}),1.0]])]});}
            var Q11;
            {var subQ0=sQuery(id+"F25.wireOp",EDGE,"QSQis5DJ-ndRP-tXz9-sWgT-VjHo9YrmBDyp.top");var subQ1=sQuery(id+"F25.wireOp",EDGE,"15366a01-08b8-4944-8cce-0e4f2887150d.0");var subQ2=makeQuery(id+"F25.imprint","INTERSECT",VERTEX,{"disambiguationData":[OD(1.0)],"derivedFrom":[subQ1,subQ0]});Q11=makeQuery(id+"F25.imprint","IMPRINT",FACE,{"disambiguationData":[TD([[makeQuery(id+"F25.imprint","IMPRINT",EDGE,{"disambiguationData":[TD([[subQ2,-1.0]])],"derivedFrom":subQ1}),1.0]])]});}
            var Q12;
            {var subQ0=sQuery(id+"F25.wireOp",EDGE,"QSQis5DJ-ndRP-tXz9-sWgT-VjHo9YrmBDyp.left");var subQ1=sQuery(id+"F25.wireOp",EDGE,"15366a01-08b8-4944-8cce-0e4f2887150d.0");var subQ2=makeQuery(id+"F25.imprint","INTERSECT",VERTEX,{"disambiguationData":[OD(1.0)],"derivedFrom":[subQ1,subQ0]});Q12=makeQuery(id+"F25.imprint","IMPRINT",FACE,{"disambiguationData":[TD([[makeQuery(id+"F25.imprint","IMPRINT",EDGE,{"disambiguationData":[TD([[subQ2,-1.0]])],"derivedFrom":subQ1}),1.0]])]});}
            var Q13;
            Q13=makeQuery(id+"F25.imprint","IMPRINT",FACE,{"disambiguationData":[TD([[makeQuery(id+"F25.imprint","IMPRINT",EDGE,{"derivedFrom":sQuery(id+"F25.wireOp",EDGE,"E87.1.3.0")}),1.0]])]});
            var Q14;
            Q14=makeQuery(id+"F25.imprint","IMPRINT",FACE,{"disambiguationData":[TD([[makeQuery(id+"F25.imprint","IMPRINT",EDGE,{"derivedFrom":sQuery(id+"F25.wireOp",EDGE,"E87.1.5.0")}),1.0]])]});
            var Q15;
            Q15=makeQuery(id+"F25.imprint","IMPRINT",FACE,{"disambiguationData":[TD([[makeQuery(id+"F25.imprint","IMPRINT",EDGE,{"derivedFrom":sQuery(id+"F25.wireOp",EDGE,"E87.1.7.0")}),1.0]])]});
            var Q16;
            Q16=makeQuery(id+"F25.imprint","IMPRINT",FACE,{"disambiguationData":[TD([[makeQuery(id+"F25.imprint","IMPRINT",EDGE,{"derivedFrom":sQuery(id+"F25.wireOp",EDGE,"E86.1.0")}),1.0]])]});
            var Q17;
            {var subQ0=sQuery(id+"F25.wireOp",EDGE,"E88.right");var subQ1=sQuery(id+"F25.wireOp",EDGE,"E88.bottom");var subQ2=makeQuery(id+"F25.imprint","INTERSECT",VERTEX,{"derivedFrom":[subQ1,subQ0]});Q17=makeQuery(id+"F25.imprint","IMPRINT",FACE,{"disambiguationData":[TD([[makeQuery(id+"F25.imprint","IMPRINT",EDGE,{"disambiguationData":[TD([[subQ2,1.0]])],"derivedFrom":subQ1}),-1.0]])]});}
            var Q18;
            {var subQ0=sQuery(id+"F25.wireOp",EDGE,"E88.right");var subQ1=sQuery(id+"F25.wireOp",EDGE,"E88.top");var subQ2=makeQuery(id+"F25.imprint","INTERSECT",VERTEX,{"derivedFrom":[subQ1,subQ0]});Q18=makeQuery(id+"F25.imprint","IMPRINT",FACE,{"disambiguationData":[TD([[makeQuery(id+"F25.imprint","IMPRINT",EDGE,{"disambiguationData":[TD([[subQ2,1.0]])],"derivedFrom":subQ1}),1.0]])]});}
            extrude(context, id + "F27", {"entities" : qUnion([Q0, Q1, Q2, Q3, Q4, Q5, Q6, Q7, Q8, Q9, Q10, Q11, Q12, Q13, Q14, Q15, Q16, Q17, Q18]), "operationType" : NewBodyOperationType.REMOVE, "oppositeDirection" : true, "depth" : 5 * mm, "offsetDistance" : 25 * mm});
        }
        {
            var Q0;
            Q0=makeQuery(id+"F4.opExtrude","CAP_FACE",FACE,{"disambiguationData":[OSD([sQuery(id+"F3.wireOp",EDGE,"E10.0"),sQuery(id+"F3.wireOp",EDGE,"E11.0"),sQuery(id+"F3.wireOp",EDGE,"E12.0"),sQuery(id+"F3.wireOp",EDGE,"E13.0"),sQuery(id+"F3.wireOp",EDGE,"E14.0"),sQuery(id+"F3.wireOp",EDGE,"E15")])],"isStart":false});
            var sketch = newSketch(context, id + "F28", { "sketchPlane" : qUnion([Q0])});
            skCircle(sketch, "E89.0", {"center": v(-58.34, -58.34) * mm, "radius": 2 * mm});
            skCircle(sketch, "E90", {"center": v(-58.34, -58.34) * mm, "radius": 7.5 * mm});
            skSolve(sketch);
        }
        {
            var Q0;
            Q0=qSketchRegion(id+"F28",true);
            extrude(context, id + "F29", {"entities" : qUnion([Q0]), "depth" : 60 * mm, "offsetDistance" : 25 * mm});
        }
        {
            var Q0;
            Q0=makeQuery(id+"F4.opExtrude","CAP_FACE",FACE,{"disambiguationData":[OSD([sQuery(id+"F3.wireOp",EDGE,"E10.0"),sQuery(id+"F3.wireOp",EDGE,"E11.0"),sQuery(id+"F3.wireOp",EDGE,"E12.0"),sQuery(id+"F3.wireOp",EDGE,"E13.0"),sQuery(id+"F3.wireOp",EDGE,"E14.0"),sQuery(id+"F3.wireOp",EDGE,"E15")])],"isStart":false});
            var sketch = newSketch(context, id + "F30", { "sketchPlane" : qUnion([Q0])});
            skArc(sketch, "E91", {"start": v(-28.93, 63.74) * mm, "mid": v(-60.62, 35) * mm, "end": v(-69.67, -6.82) * mm});
            skArc(sketch, "E92", {"start": v(-17.77, 35.83) * mm, "mid": v(-34.64, 20) * mm, "end": v(-39.92, -2.53) * mm});
            skLineSegment(sketch, "E93", {"start": v(0, 0) * mm, "end": v(0, 70) * mm, "construction": true});
            skPoint(sketch, "E94", {"position": v(0, 40) * mm});
            skPoint(sketch, "E95", {"position": v(0, 90) * mm});
            skLineSegment(sketch, "E96", {"start": v(-22.17, 60.9) * mm, "end": v(-15.3, 42.02) * mm});
            skLineSegment(sketch, "E97.MirrorCS", {"start": v(22.17, 60.9) * mm, "end": v(15.3, 42.02) * mm});
            skLineSegment(sketch, "E98.1.0", {"start": v(-41.66, -49.65) * mm, "end": v(-28.75, -34.26) * mm});
            skLineSegment(sketch, "E98.1.1", {"start": v(-63.82, -11.25) * mm, "end": v(-44.04, -7.77) * mm});
            skLineSegment(sketch, "E98.2.0", {"start": v(63.82, -11.25) * mm, "end": v(44.04, -7.77) * mm});
            skLineSegment(sketch, "E98.2.1", {"start": v(41.66, -49.65) * mm, "end": v(28.75, -34.26) * mm});
            skArc(sketch, "E99.trimOffspring", {"start": v(69.67, -6.82) * mm, "mid": v(60.62, 35) * mm, "end": v(28.93, 63.74) * mm});
            skArc(sketch, "E100.trimOffspring", {"start": v(39.92, -2.53) * mm, "mid": v(34.64, 20) * mm, "end": v(17.77, 35.83) * mm});
            skArc(sketch, "E101.trimOffspring", {"start": v(-22.15, -33.3) * mm, "mid": v(0, -40) * mm, "end": v(22.15, -33.3) * mm});
            skArc(sketch, "E102.trimOffspring", {"start": v(-40.74, -56.93) * mm, "mid": v(0, -70) * mm, "end": v(40.74, -56.93) * mm});
            skPoint(sketch, "E103.visualSharp", {"position": v(-23.94, 65.78) * mm});
            skArc(sketch, "E103.filletArc", {"start": v(-22.17, 60.9) * mm, "mid": v(-24.93, 63.8) * mm, "end": v(-28.93, 63.74) * mm});
            skPoint(sketch, "E104.visualSharp", {"position": v(-13.68, 37.59) * mm});
            skArc(sketch, "E104.filletArc", {"start": v(-17.77, 35.83) * mm, "mid": v(-15.35, 38.46) * mm, "end": v(-15.3, 42.02) * mm});
            skPoint(sketch, "E105.visualSharp", {"position": v(13.68, 37.59) * mm});
            skArc(sketch, "E105.filletArc", {"start": v(15.3, 42.02) * mm, "mid": v(15.35, 38.46) * mm, "end": v(17.77, 35.83) * mm});
            skPoint(sketch, "E106.visualSharp", {"position": v(23.94, 65.78) * mm});
            skArc(sketch, "E106.filletArc", {"start": v(28.93, 63.74) * mm, "mid": v(24.93, 63.8) * mm, "end": v(22.17, 60.9) * mm});
            skPoint(sketch, "E107.visualSharp", {"position": v(68.94, -12.16) * mm});
            skArc(sketch, "E107.filletArc", {"start": v(63.82, -11.25) * mm, "mid": v(67.71, -10.31) * mm, "end": v(69.67, -6.82) * mm});
            skPoint(sketch, "E108.visualSharp", {"position": v(39.4, -6.95) * mm});
            skArc(sketch, "E108.filletArc", {"start": v(39.92, -2.53) * mm, "mid": v(40.98, -5.93) * mm, "end": v(44.04, -7.77) * mm});
            skPoint(sketch, "E109.visualSharp", {"position": v(-39.4, -6.95) * mm});
            skArc(sketch, "E109.filletArc", {"start": v(-44.04, -7.77) * mm, "mid": v(-40.98, -5.93) * mm, "end": v(-39.92, -2.53) * mm});
            skPoint(sketch, "E110.visualSharp", {"position": v(-68.94, -12.16) * mm});
            skArc(sketch, "E110.filletArc", {"start": v(-69.67, -6.82) * mm, "mid": v(-67.71, -10.31) * mm, "end": v(-63.82, -11.25) * mm});
            skPoint(sketch, "E111.visualSharp", {"position": v(-25.71, -30.64) * mm});
            skArc(sketch, "E111.filletArc", {"start": v(-22.15, -33.3) * mm, "mid": v(-25.63, -32.52) * mm, "end": v(-28.75, -34.26) * mm});
            skPoint(sketch, "E112.visualSharp", {"position": v(-45, -53.62) * mm});
            skArc(sketch, "E112.filletArc", {"start": v(-41.66, -49.65) * mm, "mid": v(-42.79, -53.49) * mm, "end": v(-40.74, -56.93) * mm});
            skPoint(sketch, "E113.visualSharp", {"position": v(25.71, -30.64) * mm});
            skArc(sketch, "E113.filletArc", {"start": v(28.75, -34.26) * mm, "mid": v(25.63, -32.52) * mm, "end": v(22.15, -33.3) * mm});
            skPoint(sketch, "E114.visualSharp", {"position": v(45, -53.62) * mm});
            skArc(sketch, "E114.filletArc", {"start": v(40.74, -56.93) * mm, "mid": v(42.79, -53.49) * mm, "end": v(41.66, -49.65) * mm});
            skCircle(sketch, "E115.0", {"center": v(58.34, 58.34) * mm, "radius": 2 * mm});
            skCircle(sketch, "E116.1.0", {"center": v(0, 82.5) * mm, "radius": 2 * mm});
            skCircle(sketch, "E116.2.0", {"center": v(-58.34, 58.34) * mm, "radius": 2 * mm});
            skCircle(sketch, "E117.1.3.0", {"center": v(-82.5, 0) * mm, "radius": 2 * mm});
            skCircle(sketch, "E117.1.4.0", {"center": v(-58.34, -58.34) * mm, "radius": 2 * mm});
            skCircle(sketch, "E117.1.5.0", {"center": v(0, -82.5) * mm, "radius": 2 * mm});
            skCircle(sketch, "E117.1.6.0", {"center": v(58.34, -58.34) * mm, "radius": 2 * mm});
            skCircle(sketch, "E117.1.7.0", {"center": v(82.5, 0) * mm, "radius": 2 * mm});
            skLineSegment(sketch, "E118.0", {"start": v(-13.5, 17) * mm, "end": v(-13.5, 13) * mm});
            skLineSegment(sketch, "E119.0", {"start": v(-13.5, 17) * mm, "end": v(-4.5, 17) * mm});
            skLineSegment(sketch, "E120.0", {"start": v(-4.5, 17) * mm, "end": v(-4.5, 13) * mm});
            skLineSegment(sketch, "E121.0", {"start": v(-13.5, 13) * mm, "end": v(-4.5, 13) * mm});
            skPoint(sketch, "E122.0", {"position": v(-13.5, -17) * mm});
            skLineSegment(sketch, "E123.0", {"start": v(-13.5, -17) * mm, "end": v(-13.5, -13) * mm});
            skLineSegment(sketch, "E124.0", {"start": v(-13.5, -13) * mm, "end": v(-4.5, -13) * mm});
            skLineSegment(sketch, "E125.0", {"start": v(-4.5, -17) * mm, "end": v(-4.5, -13) * mm});
            skLineSegment(sketch, "E126.0", {"start": v(-13.5, -17) * mm, "end": v(-4.5, -17) * mm});
            skLineSegment(sketch, "E127.0", {"start": v(13.5, -13) * mm, "end": v(4.5, -13) * mm});
            skLineSegment(sketch, "E128.0", {"start": v(13.5, -17) * mm, "end": v(4.5, -17) * mm});
            skLineSegment(sketch, "E129.0", {"start": v(13.5, -17) * mm, "end": v(13.5, -13) * mm});
            skLineSegment(sketch, "E130.0", {"start": v(4.5, 17) * mm, "end": v(4.5, 13) * mm});
            skLineSegment(sketch, "E131.0", {"start": v(13.5, 17) * mm, "end": v(4.5, 17) * mm});
            skLineSegment(sketch, "E132.0", {"start": v(13.5, 13) * mm, "end": v(4.5, 13) * mm});
            skLineSegment(sketch, "E133.0", {"start": v(13.5, 17) * mm, "end": v(13.5, 13) * mm});
            skCircle(sketch, "E134", {"center": v(0, 27.35) * mm, "radius": 6.25 * mm});
            skLineSegment(sketch, "E135", {"start": v(4.5, -13) * mm, "end": v(4.5, -17) * mm});
            skSolve(sketch);
        }
        {
            var Q0;
            Q0=qSketchRegion(id+"F30",true);
            extrude(context, id + "F31", {"entities" : qUnion([Q0]), "operationType" : NewBodyOperationType.REMOVE, "oppositeDirection" : true, "depth" : 5 * mm, "offsetDistance" : 25 * mm});
        }
        {
            var Q0;
            {var subQ0=sQuery(id+"F3.wireOp",EDGE,"E15");Q0=makeQuery(id+"F26.boolean.opBoolean","MERGE",FACE,{"derivedFrom":[makeQuery(id+"F24.opPattern","COPY",FACE,{"derivedFrom":makeQuery(id+"F4.opExtrude","CAP_FACE",FACE,{"disambiguationData":[OSD([sQuery(id+"F3.wireOp",EDGE,"E10.0"),sQuery(id+"F3.wireOp",EDGE,"E11.0"),sQuery(id+"F3.wireOp",EDGE,"E12.0"),sQuery(id+"F3.wireOp",EDGE,"E13.0"),sQuery(id+"F3.wireOp",EDGE,"E14.0"),subQ0])],"isStart":false}),"instanceName":"1"}),makeQuery(id+"F26.opExtrude","CAP_FACE",FACE,{"disambiguationData":[OSD([sQuery(id+"F25.wireOp",EDGE,"E76.0")])],"isStart":true}),makeQuery(id+"F26.opExtrude","CAP_FACE",FACE,{"disambiguationData":[OSD([sQuery(id+"F25.wireOp",EDGE,"E77.0")])],"isStart":true}),makeQuery(id+"F26.opExtrude","CAP_FACE",FACE,{"disambiguationData":[OSD([sQuery(id+"F25.wireOp",EDGE,"E78.0")])],"isStart":true}),makeQuery(id+"F26.opExtrude","CAP_FACE",FACE,{"disambiguationData":[OSD([sQuery(id+"F25.wireOp",EDGE,"E79.0")])],"isStart":true}),makeQuery(id+"F26.opExtrude","CAP_FACE",FACE,{"disambiguationData":[OSD([subQ0,sQuery(id+"F25.wireOp",EDGE,"E88.bottom"),sQuery(id+"F25.wireOp",EDGE,"E88.top"),sQuery(id+"F25.wireOp",EDGE,"E88.left")])],"isStart":true}),makeQuery(id+"F26.opExtrude","CAP_FACE",FACE,{"disambiguationData":[OSD([subQ0,sQuery(id+"F25.wireOp",EDGE,"E88.right")])],"isStart":true})]});}
            var sketch = newSketch(context, id + "F32", { "sketchPlane" : qUnion([Q0])});
            skArc(sketch, "E136", {"start": v(67.2, -6.37) * mm, "mid": v(63.43, 23.09) * mm, "end": v(47.39, 48.07) * mm});
            skArc(sketch, "E137", {"start": v(32.47, -1.33) * mm, "mid": v(30.54, 11.12) * mm, "end": v(24.02, 21.89) * mm});
            skLineSegment(sketch, "E138", {"start": v(0, 0) * mm, "end": v(0, 67.5) * mm, "construction": true});
            skPoint(sketch, "E139", {"position": v(0, 32.5) * mm});
            skLineSegment(sketch, "E140", {"start": v(36.6, -6.45) * mm, "end": v(61.35, -10.82) * mm});
            skLineSegment(sketch, "E141", {"start": v(12.71, -34.92) * mm, "end": v(21.3, -58.54) * mm});
            skLineSegment(sketch, "E142.MirrorCS", {"start": v(0, 0) * mm, "end": v(0, -67.5) * mm, "construction": true});
            skLineSegment(sketch, "E143.1.0", {"start": v(23.89, 28.47) * mm, "end": v(40.05, 47.72) * mm});
            skLineSegment(sketch, "E143.1.1", {"start": v(-12.71, 34.92) * mm, "end": v(-21.3, 58.54) * mm});
            skLineSegment(sketch, "E143.2.0", {"start": v(-36.6, 6.45) * mm, "end": v(-61.35, 10.82) * mm});
            skLineSegment(sketch, "E143.2.1", {"start": v(-23.89, -28.47) * mm, "end": v(-40.05, -47.72) * mm});
            skArc(sketch, "E144.trimOffspring", {"start": v(-39.11, -55.01) * mm, "mid": v(-11.72, -66.47) * mm, "end": v(17.94, -65.07) * mm});
            skArc(sketch, "E145.trimOffspring", {"start": v(-17.38, -27.46) * mm, "mid": v(-5.64, -32) * mm, "end": v(6.94, -31.75) * mm});
            skArc(sketch, "E146.trimOffspring", {"start": v(-28.09, 61.38) * mm, "mid": v(-51.7, 43.39) * mm, "end": v(-65.32, 17) * mm});
            skArc(sketch, "E147.trimOffspring", {"start": v(-15.09, 28.79) * mm, "mid": v(-24.9, 20.9) * mm, "end": v(-30.97, 9.86) * mm});
            skLineSegment(sketch, "E148", {"start": v(-32, 5.64) * mm, "end": v(-20.9, -24.9) * mm, "construction": true});
            skLineSegment(sketch, "E149", {"start": v(0, 0) * mm, "end": v(-26.45, -9.63) * mm, "construction": true});
            skCircle(sketch, "E150", {"center": v(-18.8, -6.84) * mm, "radius": 6.25 * mm});
            skPoint(sketch, "E151.visualSharp", {"position": v(-66.47, 11.72) * mm});
            skArc(sketch, "E151.filletArc", {"start": v(-65.32, 17) * mm, "mid": v(-64.7, 13.04) * mm, "end": v(-61.35, 10.82) * mm});
            skPoint(sketch, "E152.visualSharp", {"position": v(-32, 5.64) * mm});
            skArc(sketch, "E152.filletArc", {"start": v(-36.6, 6.45) * mm, "mid": v(-33.14, 7.1) * mm, "end": v(-30.97, 9.86) * mm});
            skPoint(sketch, "E153.visualSharp", {"position": v(-11.12, 30.54) * mm});
            skArc(sketch, "E153.filletArc", {"start": v(-15.09, 28.79) * mm, "mid": v(-12.75, 31.4) * mm, "end": v(-12.71, 34.92) * mm});
            skPoint(sketch, "E154.visualSharp", {"position": v(20.9, 24.9) * mm});
            skArc(sketch, "E154.filletArc", {"start": v(23.89, 28.47) * mm, "mid": v(22.72, 25.15) * mm, "end": v(24.02, 21.89) * mm});
            skPoint(sketch, "E155.visualSharp", {"position": v(32, -5.64) * mm});
            skArc(sketch, "E155.filletArc", {"start": v(32.47, -1.33) * mm, "mid": v(33.57, -4.66) * mm, "end": v(36.6, -6.45) * mm});
            skPoint(sketch, "E156.visualSharp", {"position": v(43.39, 51.7) * mm});
            skArc(sketch, "E156.filletArc", {"start": v(47.39, 48.07) * mm, "mid": v(43.64, 49.5) * mm, "end": v(40.05, 47.72) * mm});
            skPoint(sketch, "E157.visualSharp", {"position": v(66.47, -11.72) * mm});
            skArc(sketch, "E157.filletArc", {"start": v(61.35, -10.82) * mm, "mid": v(65.25, -9.87) * mm, "end": v(67.2, -6.37) * mm});
            skPoint(sketch, "E158.visualSharp", {"position": v(11.12, -30.54) * mm});
            skArc(sketch, "E158.filletArc", {"start": v(12.71, -34.92) * mm, "mid": v(10.42, -32.25) * mm, "end": v(6.94, -31.75) * mm});
            skPoint(sketch, "E159.visualSharp", {"position": v(-20.9, -24.9) * mm});
            skArc(sketch, "E159.filletArc", {"start": v(-17.38, -27.46) * mm, "mid": v(-20.83, -26.74) * mm, "end": v(-23.89, -28.47) * mm});
            skPoint(sketch, "E160.visualSharp", {"position": v(-43.39, -51.7) * mm});
            skArc(sketch, "E160.filletArc", {"start": v(-40.05, -47.72) * mm, "mid": v(-41.17, -51.57) * mm, "end": v(-39.11, -55.01) * mm});
            skPoint(sketch, "E161.visualSharp", {"position": v(23.09, -63.43) * mm});
            skArc(sketch, "E161.filletArc", {"start": v(17.94, -65.07) * mm, "mid": v(21.05, -62.55) * mm, "end": v(21.3, -58.54) * mm});
            skPoint(sketch, "E162.visualSharp", {"position": v(-23.09, 63.43) * mm});
            skArc(sketch, "E162.filletArc", {"start": v(-21.3, 58.54) * mm, "mid": v(-24.08, 61.44) * mm, "end": v(-28.09, 61.38) * mm});
            skSolve(sketch);
        }
        {
            var Q0;
            Q0=qSketchRegion(id+"F32",true);
            extrude(context, id + "F33", {"entities" : qUnion([Q0]), "operationType" : NewBodyOperationType.REMOVE, "endBound" : BoundingType.UP_TO_NEXT, "oppositeDirection" : true, "depth" : 25 * mm, "offsetDistance" : 25 * mm});
        }
        {
            var Q0;
            {var subQ0=sQuery(id+"F3.wireOp",EDGE,"E15");var subQ1=sQuery(id+"F3.wireOp",EDGE,"E14.0");var subQ2=sQuery(id+"F3.wireOp",EDGE,"E13.0");var subQ3=sQuery(id+"F3.wireOp",EDGE,"E12.0");var subQ4=sQuery(id+"F3.wireOp",EDGE,"E11.0");var subQ5=sQuery(id+"F3.wireOp",EDGE,"E10.0");Q0=makeQuery(id+"F14.boolean.opBoolean","MERGE",FACE,{"derivedFrom":[makeQuery(id+"F10.opPattern","COPY",FACE,{"derivedFrom":makeQuery(id+"F4.opExtrude","CAP_FACE",FACE,{"disambiguationData":[OSD([subQ5,subQ4,subQ3,subQ2,subQ1,subQ0])],"isStart":true}),"instanceName":"1"}),makeQuery(id+"F14.opExtrude","CAP_FACE",FACE,{"disambiguationData":[OSD([subQ5,subQ4,subQ3,subQ2,subQ1,subQ0]),OD(0.0)],"isStart":false}),makeQuery(id+"F14.opExtrude","CAP_FACE",FACE,{"disambiguationData":[OSD([subQ5,subQ4,subQ3,subQ2,subQ1,subQ0]),OD(1.0)],"isStart":false}),makeQuery(id+"F14.opExtrude","CAP_FACE",FACE,{"disambiguationData":[OSD([subQ5,subQ4,subQ3,subQ2,subQ1,subQ0]),OD(2.0)],"isStart":false}),makeQuery(id+"F14.opExtrude","CAP_FACE",FACE,{"disambiguationData":[OSD([subQ5,subQ4,subQ3,subQ2,subQ1,subQ0]),OD(3.0)],"isStart":false})]});}
            var sketch = newSketch(context, id + "F34", { "sketchPlane" : qUnion([Q0])});
            skCircle(sketch, "E163", {"center": v(70, 0) * mm, "radius": 5 * mm});
            skCircle(sketch, "E164", {"center": v(70, 0) * mm, "radius": 4.5 * mm});
            skSolve(sketch);
        }
        {
            var Q0;
            Q0 = qSketchRegion(id + "F34", true);
            extrude(context, id + "F35", {"entities" : qUnion([Q0]), "depth" : 150 * mm, "offsetDistance" : 25 * mm});
        }
        {
            var Q0;
            Q0=qCreatedBy(makeId("Front.planeOp"),FACE);
            var sketch = newSketch(context, id + "F36", { "sketchPlane" : qUnion([Q0])});
            skLineSegment(sketch, "E165.0", {"start": v(75, -121) * mm, "end": v(65, -121) * mm, "construction": true});
            skLineSegment(sketch, "E166.0", {"start": v(90, 29) * mm, "end": v(-90, 29) * mm, "construction": true});
            skLineSegment(sketch, "E167", {"start": v(70, -121) * mm, "end": v(70, 29) * mm, "construction": true});
            skLineSegment(sketch, "E168", {"start": v(70, -61) * mm, "end": v(125, -61) * mm});
            skLineSegment(sketch, "E169", {"start": v(140, -76) * mm, "end": v(140, -91) * mm});
            skPoint(sketch, "E170.visualSharp", {"position": v(140, -61) * mm});
            skArc(sketch, "E170.filletArc", {"start": v(140, -76) * mm, "mid": v(135.6, -65.4) * mm, "end": v(125, -61) * mm});
            skSolve(sketch);
        }
        {
            var Q0;
            Q0=qCreatedBy(makeId("Right.planeOp"),FACE);
            cPlane(context, id + "F37", {"entities" : qUnion([Q0]), "cplaneType" : CPlaneType.OFFSET, "offset" : 70 * mm, "width" : 150 * mm, "height" : 150 * mm});
        }
        {
            var Q0;
            Q0=qCreatedBy(id+"F37.planeOp",FACE);
            var sketch = newSketch(context, id + "F38", { "sketchPlane" : qUnion([Q0])});
            skPoint(sketch, "E171.0", {"position": v(0, -61) * mm});
            skCircle(sketch, "E172", {"center": v(0, -61) * mm, "radius": 5 * mm});
            skCircle(sketch, "E173", {"center": v(0, -61) * mm, "radius": 4.5 * mm});
            skSolve(sketch);
        }
        {
            var Q0;
            Q0 = qSketchRegion(id + "F38", true);
            var Q1;
            Q1=sQuery(id+"F36.wireOp",EDGE,"E168");
            var Q2;
            Q2=sQuery(id+"F36.wireOp",EDGE,"E170.filletArc");
            var Q3;
            Q3=sQuery(id+"F36.wireOp",EDGE,"E169");
            sweep(context, id + "F39", {"operationType" : NewBodyOperationType.ADD, "profiles" : qUnion([Q0]), "path" : qUnion([Q1, Q2, Q3])});
        }
        {
            var Q0;
            Q0=makeQuery(id+"F34.imprint","IMPRINT",FACE,{"disambiguationData":[TD([[makeQuery(id+"F34.imprint","IMPRINT",EDGE,{"derivedFrom":sQuery(id+"F34.wireOp",EDGE,"E164")}),1.0]])]});
            extrude(context, id + "F40", {"entities" : qUnion([Q0]), "operationType" : NewBodyOperationType.REMOVE, "endBound" : BoundingType.THROUGH_ALL, "depth" : 25 * mm, "offsetDistance" : 25 * mm});
        }
        {
            var Q0;
            Q0=makeQuery(id+"F1.opExtrude","SWEPT_BODY",BODY,{"disambiguationData":[OSD([sQuery(id+"F0.wireOp",EDGE,"E0"),sQuery(id+"F0.wireOp",EDGE,"E1"),sQuery(id+"F0.wireOp",EDGE,"E6"),sQuery(id+"F0.wireOp",EDGE,"E7.MirrorC"),sQuery(id+"F0.wireOp",EDGE,"E8.MirrorC"),sQuery(id+"F0.wireOp",EDGE,"E9.MirrorC")])]});
            transform(context, id + "F41", {"entities" : qUnion([Q0]), "transformType" : TransformType.TRANSLATION_3D, "dx" : 0 * mm, "dy" : 0 * mm, "dz" : 50 * mm, "makeCopy" : false});
        }
        {
            var Q0;
            Q0=makeQuery(id+"F1.opExtrude","CAP_FACE",FACE,{"disambiguationData":[OSD([sQuery(id+"F0.wireOp",EDGE,"E0"),sQuery(id+"F0.wireOp",EDGE,"E1"),sQuery(id+"F0.wireOp",EDGE,"E6"),sQuery(id+"F0.wireOp",EDGE,"E7.MirrorC"),sQuery(id+"F0.wireOp",EDGE,"E8.MirrorC"),sQuery(id+"F0.wireOp",EDGE,"E9.MirrorC")])],"isStart":false});
            var sketch = newSketch(context, id + "F42", { "sketchPlane" : qUnion([Q0])});
            skCircle(sketch, "E174.0", {"center": v(0, 0) * mm, "radius": 90 * mm});
            skCircle(sketch, "E175", {"center": v(0, 0) * mm, "radius": 65 * mm});
            skCircle(sketch, "E176", {"center": v(0, 0) * mm, "radius": 30 * mm});
            skSolve(sketch);
        }
        {
            var Q0;
            Q0 = qSketchRegion(id + "F42", true);
            var Q1;
            Q1=makeQuery(id+"F42.imprint","IMPRINT",FACE,{"disambiguationData":[TD([[makeQuery(id+"F42.imprint","IMPRINT",EDGE,{"derivedFrom":sQuery(id+"F42.wireOp",EDGE,"E176")}),1.0]])]});
            extrude(context, id + "F43", {"entities" : qUnion([Q0, Q1]), "operationType" : NewBodyOperationType.ADD, "depth" : 2 * mm, "offsetDistance" : 25 * mm});
        }
        {
            var Q0;
            Q0=makeQuery(id+"F43.opExtrude","CAP_FACE",FACE,{"disambiguationData":[OSD([sQuery(id+"F42.wireOp",EDGE,"E174.0"),sQuery(id+"F42.wireOp",EDGE,"E175")])],"isStart":false});
            var sketch = newSketch(context, id + "F44", { "sketchPlane" : qUnion([Q0])});
            skCircle(sketch, "E177.0", {"center": v(0, 0) * mm, "radius": 65 * mm});
            skCircle(sketch, "E178", {"center": v(0, 0) * mm, "radius": 74.8 * mm});
            skSolve(sketch);
        }
        {
            var Q0;
            Q0 = qSketchRegion(id + "F44", true);
            extrude(context, id + "F45", {"entities" : qUnion([Q0]), "depth" : 2 * mm, "offsetDistance" : 25 * mm});
        }
    });
